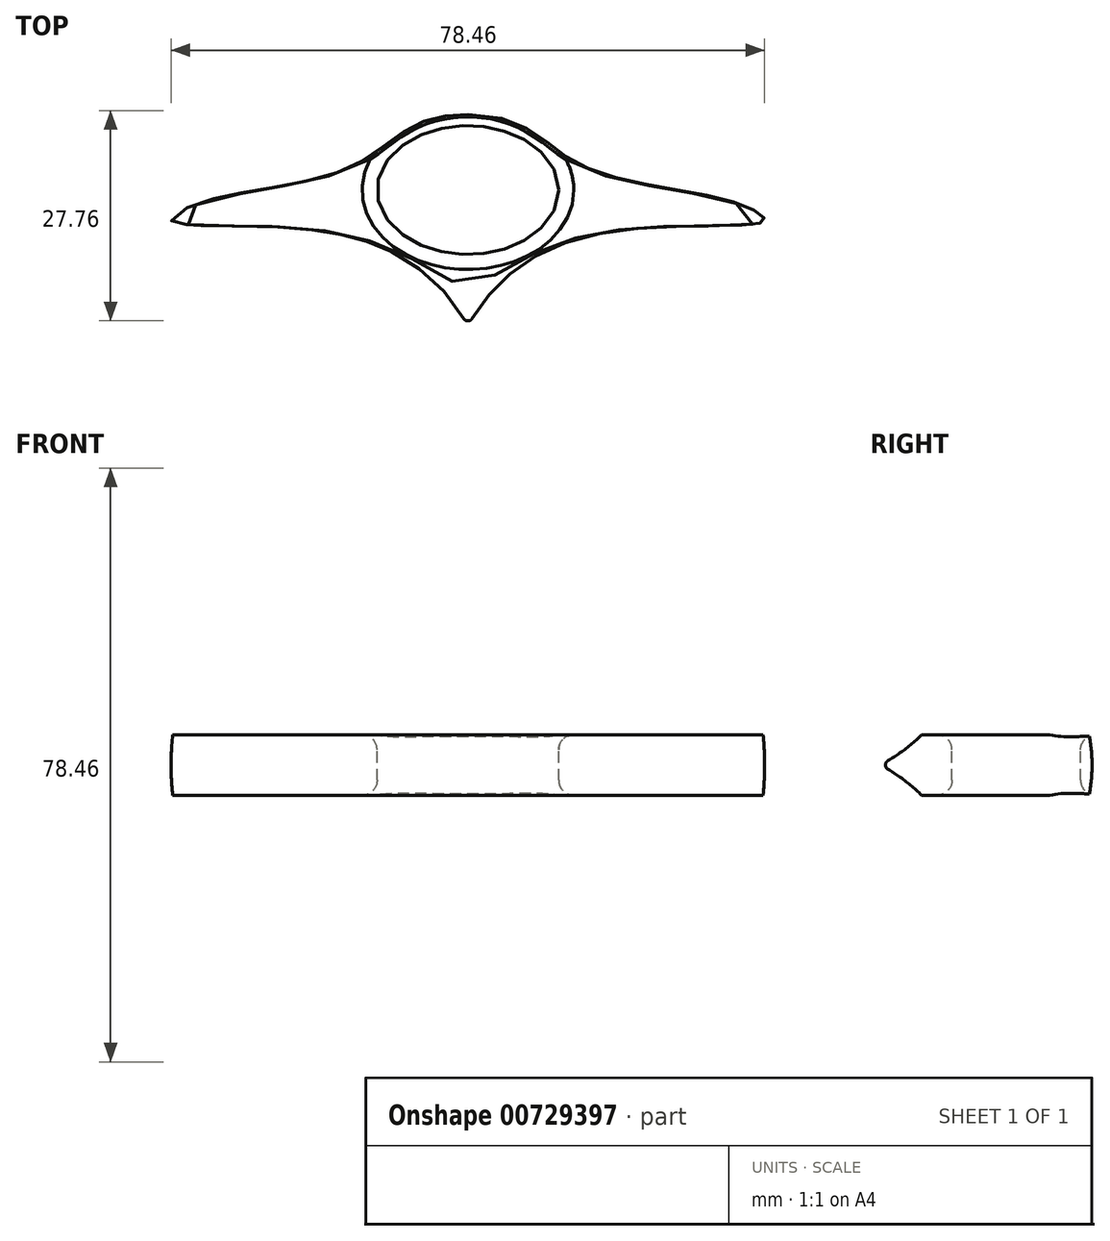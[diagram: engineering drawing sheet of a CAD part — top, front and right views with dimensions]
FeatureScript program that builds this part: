
annotation { "Feature Type Name" : "Feature", "Feature Type Description" : "" }
export const myFeature = defineFeature(function(context is Context, id is Id, definition is map)
    precondition{}
    {
        {
            var Q0;
            Q0=qCreatedBy(makeId("Top.planeOp"),FACE);
            var sketch = newSketch(context, id + "F0", { "sketchPlane" : qUnion([Q0])});
            skEllipse(sketch, "E0", {"center": v(0, 0) * mm, "majorRadius": 12 * mm, "minorRadius": 8.5 * mm, "majorAxis": v(1, 0)});
            skLineSegment(sketch, "E1", {"start": v(-12, 0) * mm, "end": v(12, 0) * mm});
            skLineSegment(sketch, "E2", {"start": v(0, 8.5) * mm, "end": v(0, -8.5) * mm});
            skSolve(sketch);
        }
        {
            var Q0;
            Q0=qCreatedBy(makeId("Top.planeOp"),FACE);
            var sketch = newSketch(context, id + "F1", { "sketchPlane" : qUnion([Q0])});
            skPoint(sketch, "E3.middle", {"position": v(0, 0) * mm});
            skLineSegment(sketch, "E4", {"start": v(-34.97, -1.54) * mm, "end": v(0, 0) * mm});
            skLineSegment(sketch, "E5", {"start": v(0, 0) * mm, "end": v(0, 10) * mm});
            skFitSpline(sketch, "E6", {"points": [v(0, 10) * mm, v(-14.86, 3.32) * mm, v(-34.97, -1.54) * mm, v(-39.15, -4.1) * mm, v(-17.97, -5.63) * mm, v(0, -18) * mm], "startDerivative": vector(-122.45, 0.25) * mm, "endDerivative": vector(42.34, -81.13) * mm});
            skFitSpline(sketch, "E7.MirrorCS", {"points": [v(0, 10) * mm, v(14.86, 3.32) * mm, v(34.97, -1.54) * mm, v(39.15, -4.1) * mm, v(17.97, -5.63) * mm, v(0, -18) * mm], "startDerivative": vector(122.45, 0.25) * mm, "endDerivative": vector(-42.34, -81.13) * mm});
            skLineSegment(sketch, "E8", {"start": v(0, 0) * mm, "end": v(0, -18) * mm});
            skLineSegment(sketch, "E9", {"start": v(0, 10) * mm, "end": v(0, -18) * mm});
            skSolve(sketch);
        }
        {
            var Q0;
            Q0=makeQuery(id+"F1.imprint","IMPRINT",FACE,{"disambiguationData":[TD([[makeQuery(id+"F1.imprint","IMPRINT",EDGE,{"derivedFrom":sQuery(id+"F1.wireOp",EDGE,"E5")}),-1.0]])]});
            var Q1;
            Q1=sQuery(id+"F1.wireOp",EDGE,"E9");
            revolve(context, id + "F2", {"surfaceOperationType" : NewSurfaceOperationType.NEW, "entities" : qUnion([Q0]), "axis" : qUnion([Q1]), "revolveType" : RevolveType.FULL});
        }
        {
            var Q0;
            Q0=qCreatedBy(makeId("Top.planeOp"),FACE);
            var sketch = newSketch(context, id + "F3", { "sketchPlane" : qUnion([Q0])});
            skLineSegment(sketch, "E10.bottom", {"start": v(-44.72, 22.25) * mm, "end": v(45.08, 22.25) * mm});
            skLineSegment(sketch, "E10.top", {"start": v(-44.72, -23.04) * mm, "end": v(45.08, -23.04) * mm});
            skLineSegment(sketch, "E10.left", {"start": v(-44.72, 22.25) * mm, "end": v(-44.72, -23.04) * mm});
            skLineSegment(sketch, "E10.right", {"start": v(45.08, 22.25) * mm, "end": v(45.08, -23.04) * mm});
            skSolve(sketch);
        }
        {
            var Q0;
            Q0=makeQuery(id+"F3.imprint","IMPRINT",FACE,{"disambiguationData":[TD([[makeQuery(id+"F3.imprint","IMPRINT",EDGE,{"derivedFrom":sQuery(id+"F3.wireOp",EDGE,"E10.bottom")}),-1.0]])]});
            extrude(context, id + "F4", {"entities" : qUnion([Q0]), "depth" : 8 * mm, "offsetDistance" : 25 * mm});
        }
        {
            var Q0;
            Q0=makeQuery(id+"F4.opExtrude","SWEPT_BODY",BODY,{"disambiguationData":[OSD([sQuery(id+"F3.wireOp",EDGE,"E10.bottom"),sQuery(id+"F3.wireOp",EDGE,"E10.top"),sQuery(id+"F3.wireOp",EDGE,"E10.left"),sQuery(id+"F3.wireOp",EDGE,"E10.right")])]});
            transform(context, id + "F5", {"entities" : qUnion([Q0]), "transformType" : TransformType.TRANSLATION_3D, "dx" : 0 * mm, "dy" : 0 * mm, "dz" : -4 * mm, "makeCopy" : false});
        }
        {
            var Q0;
            Q0=makeQuery(id+"F4.opExtrude","SWEPT_BODY",BODY,{"disambiguationData":[OSD([sQuery(id+"F3.wireOp",EDGE,"E10.bottom"),sQuery(id+"F3.wireOp",EDGE,"E10.top"),sQuery(id+"F3.wireOp",EDGE,"E10.left"),sQuery(id+"F3.wireOp",EDGE,"E10.right")])]});
            var Q1;
            Q1=makeQuery(id+"F2.opRevolve","SWEPT_BODY",BODY,{"disambiguationData":[OSD([sQuery(id+"F1.wireOp",EDGE,"E5"),sQuery(id+"F1.wireOp",EDGE,"E7.MirrorCS"),sQuery(id+"F1.wireOp",EDGE,"E8")])]});
            booleanBodies(context, id + "F6", {"operationType" : BooleanOperationType.INTERSECTION, "tools" : qUnion([Q0, Q1])});
        }
        {
            var Q0;
            Q0 = qSketchRegion(id + "F0", true);
            extrude(context, id + "F7", {"entities" : qUnion([Q0]), "operationType" : NewBodyOperationType.REMOVE, "oppositeDirection" : true, "depth" : 25 * mm, "offsetDistance" : 25 * mm});
        }
        {
            var Q0;
            Q0 = qSketchRegion(id + "F0", true);
            extrude(context, id + "F8", {"entities" : qUnion([Q0]), "operationType" : NewBodyOperationType.REMOVE, "oppositeDirection" : true, "depth" : -25 * mm, "offsetDistance" : 25 * mm});
        }
        {
            var Q0;
            Q0=makeQuery(id+"F8.boolean.opBoolean","INTERSECT",EDGE,{"derivedFrom":[makeQuery(id+"F4.opExtrude","CAP_FACE",FACE,{"disambiguationData":[OSD([sQuery(id+"F3.wireOp",EDGE,"E10.bottom"),sQuery(id+"F3.wireOp",EDGE,"E10.top"),sQuery(id+"F3.wireOp",EDGE,"E10.left"),sQuery(id+"F3.wireOp",EDGE,"E10.right")])],"isStart":false}),makeQuery(id+"F8.opExtrude","SWEPT_FACE",FACE,{"disambiguationData":[OSD([sQuery(id+"F0.wireOp",EDGE,"E0")])]})]});
            var Q1;
            Q1=makeQuery(id+"F7.boolean.opBoolean","INTERSECT",EDGE,{"derivedFrom":[makeQuery(id+"F4.opExtrude","CAP_FACE",FACE,{"disambiguationData":[OSD([sQuery(id+"F3.wireOp",EDGE,"E10.bottom"),sQuery(id+"F3.wireOp",EDGE,"E10.top"),sQuery(id+"F3.wireOp",EDGE,"E10.left"),sQuery(id+"F3.wireOp",EDGE,"E10.right")])],"isStart":true}),makeQuery(id+"F7.opExtrude","SWEPT_FACE",FACE,{"disambiguationData":[OSD([sQuery(id+"F0.wireOp",EDGE,"E0")])]})]});
            fillet(context, id + "F9", {"entities" : qUnion([Q0, Q1]), "radius" : 2 * mm, "tangentPropagation" : true, "allowEdgeOverflow" : false});
        }
        {
            var Q0;
            Q0=qCreatedBy(makeId("Top.planeOp"),FACE);
            var sketch = newSketch(context, id + "F10", { "sketchPlane" : qUnion([Q0])});
            skLineSegment(sketch, "E11.bottom", {"start": v(-3.74, -17.26) * mm, "end": v(3.53, -17.26) * mm});
            skLineSegment(sketch, "E11.top", {"start": v(-3.74, -20.83) * mm, "end": v(3.53, -20.83) * mm});
            skLineSegment(sketch, "E11.left", {"start": v(-3.74, -17.26) * mm, "end": v(-3.74, -20.83) * mm});
            skLineSegment(sketch, "E11.right", {"start": v(3.53, -17.26) * mm, "end": v(3.53, -20.83) * mm});
            skSolve(sketch);
        }
        {
            var Q0;
            Q0=makeQuery(id+"F10.imprint","IMPRINT",FACE,{"disambiguationData":[TD([[makeQuery(id+"F10.imprint","IMPRINT",EDGE,{"derivedFrom":sQuery(id+"F10.wireOp",EDGE,"E11.bottom")}),-1.0]])]});
            var Q1;
            Q1=sQuery(id+"F10.wireOp",EDGE,"E11.right");
            revolve(context, id + "F11", {"surfaceOperationType" : NewSurfaceOperationType.NEW, "entities" : qUnion([Q0]), "axis" : qUnion([Q1]), "revolveType" : RevolveType.FULL});
        }
        {
            var Q0;
            Q0=makeQuery(id+"F11.opRevolve","SWEPT_BODY",BODY,{"disambiguationData":[OSD([sQuery(id+"F10.wireOp",EDGE,"E11.bottom"),sQuery(id+"F10.wireOp",EDGE,"E11.top"),sQuery(id+"F10.wireOp",EDGE,"E11.left"),sQuery(id+"F10.wireOp",EDGE,"E11.right")])]});
            var Q1;
            Q1=makeQuery(id+"F6.opBoolean","INTERSECT",BODY,{"derivedFrom":[makeQuery(id+"F2.opRevolve","SWEPT_BODY",BODY,{"disambiguationData":[OSD([sQuery(id+"F1.wireOp",EDGE,"E5"),sQuery(id+"F1.wireOp",EDGE,"E7.MirrorCS"),sQuery(id+"F1.wireOp",EDGE,"E8")])]}),makeQuery(id+"F4.opExtrude","SWEPT_BODY",BODY,{"disambiguationData":[OSD([sQuery(id+"F3.wireOp",EDGE,"E10.bottom"),sQuery(id+"F3.wireOp",EDGE,"E10.top"),sQuery(id+"F3.wireOp",EDGE,"E10.left"),sQuery(id+"F3.wireOp",EDGE,"E10.right")])]})]});
            booleanBodies(context, id + "F12", {"operationType" : BooleanOperationType.SUBTRACTION, "tools" : qUnion([Q0]), "targets" : qUnion([Q1])});
        }
        {
            var Q0;
            Q0=makeQuery(id+"F12.opBoolean","INTERSECT",EDGE,{"derivedFrom":[makeQuery(id+"F2.opRevolve","SWEPT_FACE",FACE,{"disambiguationData":[OSD([sQuery(id+"F1.wireOp",EDGE,"E7.MirrorCS")])]}),makeQuery(id+"F11.opRevolve","SWEPT_FACE",FACE,{"disambiguationData":[OSD([sQuery(id+"F10.wireOp",EDGE,"E11.bottom")])]})]});
            fillet(context, id + "F13", {"entities" : qUnion([Q0]), "radius" : 0.5 * mm, "tangentPropagation" : true, "allowEdgeOverflow" : false});
        }
    });
